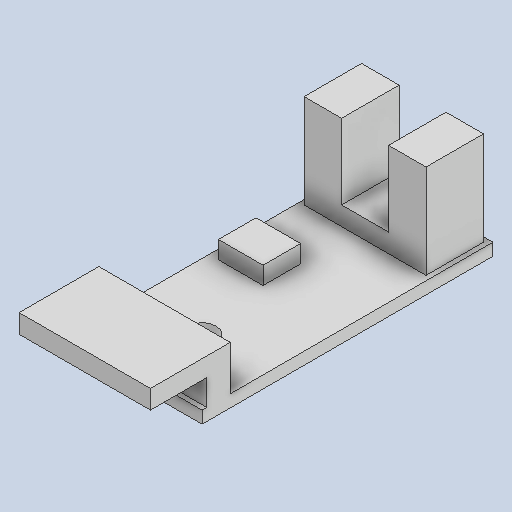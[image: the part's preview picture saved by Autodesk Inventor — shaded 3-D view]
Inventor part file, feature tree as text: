
AUTODESK INVENTOR PART (.ipt)
format: ipt  version: 2022 (Build 260153070, 153G)  size: 160,768 bytes
history: native  units: in
note: dims shown in document units (in); Inventor stores cm internally (conversion verified against a paired STEP export)
features: extrude x5, sketch x3
ambient origin geometry x8: Origin, YZ Plane, XZ Plane, XY Plane, X Axis, Y Axis, Z Axis, Center Point
bodies: Solid1 (feature_tree)
feature tree (8):
  sketch  "Sketch1"  dims[d0=0.5512in d1=1.2205in]
  extrude  "Extrusion1"  Depth=1.2205in
  extrude  "Extrusion2"  Depth=0.5118in
  extrude  "Extrusion3"  Depth=0.0197in
  extrude  "Extrusion4"  Depth=0.1181in
  extrude  "Extrusion5"  Depth=0.315in
  sketch  "Sketch2"  dims[d2=0.0197in d3=0.5118in]
  sketch  "Sketch3"  dims[d4=0.2411in d5=0.0197in d7=0.1181in d8=0.2756in d9=0.0394in d10=0.5807in d11=0.1575in d12=0.187in d13=0.0512in d14=0.0in d15=0.0787in d16=0.0in d17=0.0738in d18=0.0in d19=0.1575in d20=0.1575in d21=0.315in d22=0.0in d23=0.187in d24=0.0984in d25=0.0197in d26=0.3346in d27=0.0787in d28=0.315in d29=0.0in]
